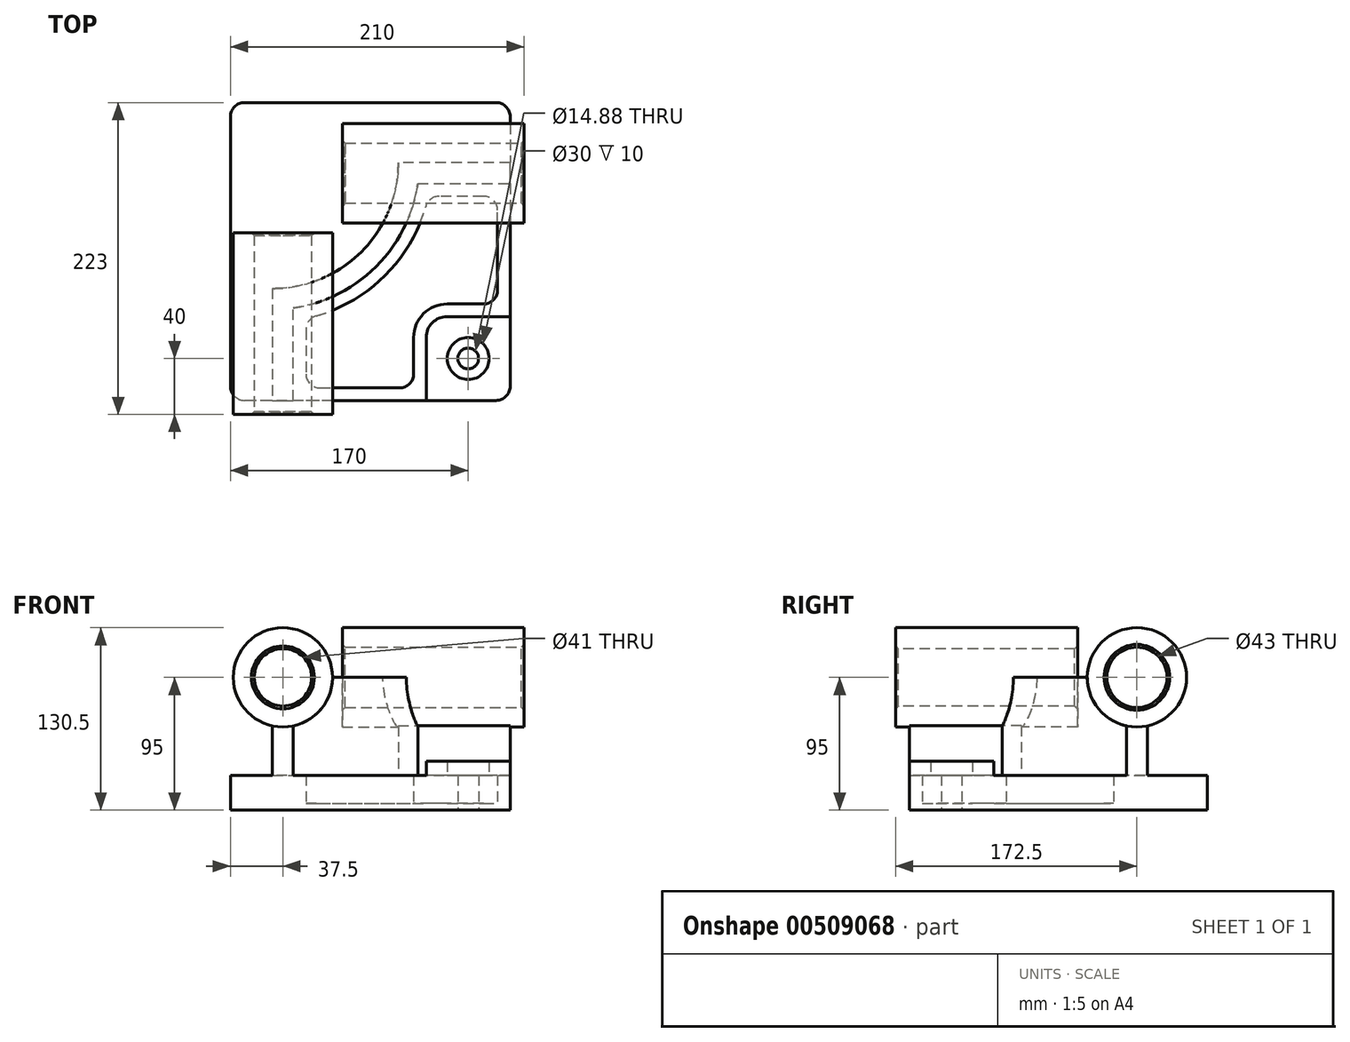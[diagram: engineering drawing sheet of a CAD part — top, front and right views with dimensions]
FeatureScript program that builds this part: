
annotation { "Feature Type Name" : "Feature", "Feature Type Description" : "" }
export const myFeature = defineFeature(function(context is Context, id is Id, definition is map)
    precondition{}
    {
        {
            var Q0;
            Q0=qCreatedBy(makeId("Top.planeOp"),FACE);
            var sketch = newSketch(context, id + "F0", { "sketchPlane" : qUnion([Q0])});
            skLineSegment(sketch, "E0.bottom", {"start": v(-10, 0) * mm, "end": v(-190, 0) * mm});
            skLineSegment(sketch, "E0.top", {"start": v(-10, -213) * mm, "end": v(-190, -213) * mm});
            skLineSegment(sketch, "E0.left", {"start": v(0, -10) * mm, "end": v(0, -203) * mm});
            skLineSegment(sketch, "E0.right", {"start": v(-200, -10) * mm, "end": v(-200, -203) * mm});
            skPoint(sketch, "E1.visualSharp", {"position": v(-200, -213) * mm});
            skArc(sketch, "E1.filletArc", {"start": v(-200, -203) * mm, "mid": v(-197.07, -210.07) * mm, "end": v(-190, -213) * mm});
            skPoint(sketch, "E2.visualSharp", {"position": v(-200, 0) * mm});
            skArc(sketch, "E2.filletArc", {"start": v(-190, 0) * mm, "mid": v(-197.07, -2.93) * mm, "end": v(-200, -10) * mm});
            skPoint(sketch, "E3.visualSharp", {"position": v(0, 0) * mm});
            skArc(sketch, "E3.filletArc", {"start": v(0, -10) * mm, "mid": v(-2.93, -2.93) * mm, "end": v(-10, 0) * mm});
            skPoint(sketch, "E4.visualSharp", {"position": v(0, -213) * mm});
            skArc(sketch, "E4.filletArc", {"start": v(-10, -213) * mm, "mid": v(-2.93, -210.07) * mm, "end": v(0, -203) * mm});
            skSolve(sketch);
        }
        {
            var Q0;
            Q0 = qSketchRegion(id + "F0", true);
            extrude(context, id + "F1", {"entities" : qUnion([Q0]), "depth" : 25 * mm});
        }
        {
            var Q0;
            Q0=qCreatedBy(makeId("Top.planeOp"),FACE);
            var sketch = newSketch(context, id + "F2", { "sketchPlane" : qUnion([Q0])});
            skLineSegment(sketch, "E5", {"start": v(-170, -213) * mm, "end": v(-170, -133) * mm});
            skLineSegment(sketch, "E6", {"start": v(-80, -43) * mm, "end": v(0, -43) * mm});
            skLineSegment(sketch, "E7", {"start": v(0, -43) * mm, "end": v(0, -58) * mm});
            skLineSegment(sketch, "E8", {"start": v(0, -58) * mm, "end": v(-66.08, -58) * mm});
            skLineSegment(sketch, "E9", {"start": v(-155, -146.92) * mm, "end": v(-155, -213) * mm});
            skLineSegment(sketch, "E10", {"start": v(-155, -213) * mm, "end": v(-170, -213) * mm});
            skArc(sketch, "E11", {"start": v(-155, -146.92) * mm, "mid": v(-95.75, -117.25) * mm, "end": v(-66.08, -58) * mm});
            skArc(sketch, "E12", {"start": v(-170, -133) * mm, "mid": v(-106.36, -106.64) * mm, "end": v(-80, -43) * mm});
            skLineSegment(sketch, "E13", {"start": v(-170, -43) * mm, "end": v(-107.14, -107.41) * mm, "construction": true});
            skLineSegment(sketch, "E14", {"start": v(-107.14, -107.41) * mm, "end": v(-96.67, -118.15) * mm, "construction": true});
            skSolve(sketch);
        }
        {
            var Q0;
            Q0 = qSketchRegion(id + "F2", true);
            extrude(context, id + "F3", {"entities" : qUnion([Q0]), "operationType" : NewBodyOperationType.ADD, "depth" : 95 * mm});
        }
        {
            var Q0;
            Q0=makeQuery(id+"F3.boolean.opBoolean","MERGE",FACE,{"derivedFrom":[makeQuery(id+"F1.opExtrude","SWEPT_FACE",FACE,{"disambiguationData":[OSD([sQuery(id+"F0.wireOp",EDGE,"E0.top")])]}),makeQuery(id+"F3.opExtrude","SWEPT_FACE",FACE,{"disambiguationData":[OSD([sQuery(id+"F2.wireOp",EDGE,"E10")])]})]});
            cPlane(context, id + "F4", {"entities" : qUnion([Q0]), "cplaneType" : CPlaneType.OFFSET, "offset" : 10 * mm, "width" : 150 * mm, "height" : 150 * mm});
        }
        {
            var Q0;
            Q0=makeQuery(id+"F3.boolean.opBoolean","MERGE",FACE,{"derivedFrom":[makeQuery(id+"F1.opExtrude","SWEPT_FACE",FACE,{"disambiguationData":[OSD([sQuery(id+"F0.wireOp",EDGE,"E0.left")])]}),makeQuery(id+"F3.opExtrude","SWEPT_FACE",FACE,{"disambiguationData":[OSD([sQuery(id+"F2.wireOp",EDGE,"E7")])]})]});
            cPlane(context, id + "F5", {"entities" : qUnion([Q0]), "cplaneType" : CPlaneType.OFFSET, "offset" : 10 * mm, "width" : 150 * mm, "height" : 150 * mm});
        }
        {
            var Q0;
            Q0=qCreatedBy(id+"F4.planeOp",FACE);
            var sketch = newSketch(context, id + "F6", { "sketchPlane" : qUnion([Q0])});
            skCircle(sketch, "E15", {"center": v(-162.5, 95) * mm, "radius": 35.5 * mm});
            skSolve(sketch);
        }
        {
            var Q0;
            Q0 = qSketchRegion(id + "F6", true);
            extrude(context, id + "F7", {"entities" : qUnion([Q0]), "operationType" : NewBodyOperationType.ADD, "oppositeDirection" : true, "depth" : 130 * mm});
        }
        {
            var Q0;
            Q0=qCreatedBy(id+"F5.planeOp",FACE);
            var sketch = newSketch(context, id + "F8", { "sketchPlane" : qUnion([Q0])});
            skCircle(sketch, "E16", {"center": v(-50.5, 95) * mm, "radius": 35.5 * mm});
            skSolve(sketch);
        }
        {
            var Q0;
            Q0 = qSketchRegion(id + "F8", true);
            extrude(context, id + "F9", {"entities" : qUnion([Q0]), "operationType" : NewBodyOperationType.ADD, "oppositeDirection" : true, "depth" : 130 * mm});
        }
        {
            var Q0;
            Q0=makeQuery(id+"F3.opExtrude","CAP_FACE",FACE,{"disambiguationData":[OSD([sQuery(id+"F2.wireOp",EDGE,"E5"),sQuery(id+"F2.wireOp",EDGE,"E6"),sQuery(id+"F2.wireOp",EDGE,"E7"),sQuery(id+"F2.wireOp",EDGE,"E8"),sQuery(id+"F2.wireOp",EDGE,"E9"),sQuery(id+"F2.wireOp",EDGE,"E10"),sQuery(id+"F2.wireOp",EDGE,"E11"),sQuery(id+"F2.wireOp",EDGE,"E12")])],"isStart":false});
            var sketch = newSketch(context, id + "F10", { "sketchPlane" : qUnion([Q0])});
            skLineSegment(sketch, "E17.0", {"start": v(-127, -223) * mm, "end": v(-198, -223) * mm, "construction": true});
            skLineSegment(sketch, "E18.0", {"start": v(-127, -93) * mm, "end": v(-198, -93) * mm, "construction": true});
            skLineSegment(sketch, "E19", {"start": v(-162.5, -223) * mm, "end": v(-162.5, -93) * mm});
            skLineSegment(sketch, "E20", {"start": v(-162.5, -223) * mm, "end": v(-185, -223) * mm});
            skLineSegment(sketch, "E21", {"start": v(-185, -223) * mm, "end": v(-185, -93) * mm, "construction": true});
            skLineSegment(sketch, "E22", {"start": v(-185, -93) * mm, "end": v(-162.5, -93) * mm});
            skLineSegment(sketch, "E23", {"start": v(-185, -223) * mm, "end": v(-183, -221) * mm});
            skLineSegment(sketch, "E24", {"start": v(-183, -221) * mm, "end": v(-183, -95) * mm});
            skLineSegment(sketch, "E25", {"start": v(-183, -95) * mm, "end": v(-185, -93) * mm});
            skLineSegment(sketch, "E26", {"start": v(-162.5, -223) * mm, "end": v(-162.5, -264.32) * mm, "construction": true});
            skSolve(sketch);
        }
        {
            var Q0;
            Q0 = qSketchRegion(id + "F10", true);
            var Q1;
            Q1=sQuery(id+"F10.wireOp",EDGE,"E26");
            revolve(context, id + "F11", {"operationType" : NewBodyOperationType.REMOVE, "entities" : qUnion([Q0]), "axis" : qUnion([Q1]), "revolveType" : RevolveType.FULL, "oppositeDirection" : true});
        }
        {
            var Q0;
            Q0=makeQuery(id+"F3.opExtrude","CAP_FACE",FACE,{"disambiguationData":[OSD([sQuery(id+"F2.wireOp",EDGE,"E5"),sQuery(id+"F2.wireOp",EDGE,"E6"),sQuery(id+"F2.wireOp",EDGE,"E7"),sQuery(id+"F2.wireOp",EDGE,"E8"),sQuery(id+"F2.wireOp",EDGE,"E9"),sQuery(id+"F2.wireOp",EDGE,"E10"),sQuery(id+"F2.wireOp",EDGE,"E11"),sQuery(id+"F2.wireOp",EDGE,"E12")])],"isStart":false});
            var sketch = newSketch(context, id + "F12", { "sketchPlane" : qUnion([Q0])});
            skLineSegment(sketch, "E27.0", {"start": v(-120, -15) * mm, "end": v(-120, -86) * mm, "construction": true});
            skLineSegment(sketch, "E28.0", {"start": v(10, -15) * mm, "end": v(10, -86) * mm, "construction": true});
            skLineSegment(sketch, "E29", {"start": v(-120, -50.5) * mm, "end": v(10, -50.5) * mm});
            skLineSegment(sketch, "E30", {"start": v(-120, -50.5) * mm, "end": v(-120, -74) * mm});
            skLineSegment(sketch, "E31", {"start": v(-120, -74) * mm, "end": v(10, -74) * mm, "construction": true});
            skLineSegment(sketch, "E32", {"start": v(10, -74) * mm, "end": v(10, -50.5) * mm});
            skLineSegment(sketch, "E33", {"start": v(-120, -74) * mm, "end": v(-118, -72) * mm});
            skLineSegment(sketch, "E34", {"start": v(-118, -72) * mm, "end": v(8, -72) * mm});
            skLineSegment(sketch, "E35", {"start": v(8, -72) * mm, "end": v(10, -74) * mm});
            skLineSegment(sketch, "E36", {"start": v(10, -50.5) * mm, "end": v(28.45, -50.5) * mm, "construction": true});
            skSolve(sketch);
        }
        {
            var Q0;
            Q0 = qSketchRegion(id + "F12", true);
            var Q1;
            Q1=sQuery(id+"F12.wireOp",EDGE,"E36");
            revolve(context, id + "F13", {"operationType" : NewBodyOperationType.REMOVE, "entities" : qUnion([Q0]), "axis" : qUnion([Q1]), "revolveType" : RevolveType.FULL, "oppositeDirection" : true});
        }
        {
            var Q0;
            Q0=qCreatedBy(makeId("Top.planeOp"),FACE);
            var sketch = newSketch(context, id + "F14", { "sketchPlane" : qUnion([Q0])});
            skLineSegment(sketch, "E37.0", {"start": v(-10, -213) * mm, "end": v(-60, -213) * mm});
            skPoint(sketch, "E38.0", {"position": v(-2.93, -210.07) * mm});
            skLineSegment(sketch, "E39.0", {"start": v(0, -153) * mm, "end": v(0, -203) * mm});
            skArc(sketch, "E40.0", {"start": v(-10, -213) * mm, "mid": v(-2.93, -210.07) * mm, "end": v(0, -203) * mm});
            skLineSegment(sketch, "E41", {"start": v(-60, -213) * mm, "end": v(-60, -168) * mm});
            skLineSegment(sketch, "E42", {"start": v(-45, -153) * mm, "end": v(0, -153) * mm});
            skPoint(sketch, "E43.orphan", {"position": v(-155, -213) * mm});
            skArc(sketch, "E44", {"start": v(-45, -153) * mm, "mid": v(-55.6, -157.4) * mm, "end": v(-60, -168) * mm});
            skPoint(sketch, "E45.orphan", {"position": v(0, -58) * mm});
            skSolve(sketch);
        }
        {
            var Q0;
            Q0 = qSketchRegion(id + "F14", true);
            extrude(context, id + "F15", {"entities" : qUnion([Q0]), "operationType" : NewBodyOperationType.ADD, "depth" : 35 * mm});
        }
        {
            var Q0;
            Q0=qCreatedBy(makeId("Right.planeOp"),FACE);
            cPlane(context, id + "F16", {"entities" : qUnion([Q0]), "cplaneType" : CPlaneType.OFFSET, "offset" : 30 * mm, "oppositeDirection" : true, "width" : 150 * mm, "height" : 150 * mm});
        }
        {
            var Q0;
            Q0=qCreatedBy(id+"F16.planeOp",FACE);
            var sketch = newSketch(context, id + "F17", { "sketchPlane" : qUnion([Q0])});
            skLineSegment(sketch, "E46", {"start": v(-183, 79.02) * mm, "end": v(-183, -100.5) * mm});
            skLineSegment(sketch, "E47", {"start": v(-183, -100.5) * mm, "end": v(-175.56, -100.5) * mm});
            skLineSegment(sketch, "E48", {"start": v(-175.56, -100.5) * mm, "end": v(-175.56, 25) * mm});
            skLineSegment(sketch, "E49", {"start": v(-175.56, 25) * mm, "end": v(-168, 25) * mm});
            skLineSegment(sketch, "E50", {"start": v(-168, 25) * mm, "end": v(-168, 79.02) * mm});
            skLineSegment(sketch, "E51", {"start": v(-168, 79.02) * mm, "end": v(-183, 79.02) * mm});
            skLineSegment(sketch, "E52", {"start": v(-183, -100.5) * mm, "end": v(-183, -118.63) * mm, "construction": true});
            skSolve(sketch);
        }
        {
            var Q0;
            Q0 = qSketchRegion(id + "F17", true);
            var Q1;
            Q1=sQuery(id+"F17.wireOp",EDGE,"E52");
            revolve(context, id + "F18", {"operationType" : NewBodyOperationType.REMOVE, "entities" : qUnion([Q0]), "axis" : qUnion([Q1]), "revolveType" : RevolveType.FULL, "oppositeDirection" : true});
        }
        {
            var Q0;
            Q0=qCreatedBy(makeId("Top.planeOp"),FACE);
            cPlane(context, id + "F19", {"entities" : qUnion([Q0]), "cplaneType" : CPlaneType.OFFSET, "offset" : 5 * mm, "width" : 150 * mm, "height" : 150 * mm});
        }
        {
            var Q0;
            Q0=qCreatedBy(id+"F19.planeOp",FACE);
            var sketch = newSketch(context, id + "F20", { "sketchPlane" : qUnion([Q0])});
            skLineSegment(sketch, "E53.0.0", {"start": v(-45, -153) * mm, "end": v(0, -153) * mm, "construction": true});
            skLineSegment(sketch, "E53.0.1", {"start": v(0, -153) * mm, "end": v(0, -58) * mm, "construction": true});
            skLineSegment(sketch, "E53.0.2", {"start": v(0, -58) * mm, "end": v(-66.08, -58) * mm, "construction": true});
            skArc(sketch, "E53.0.3", {"start": v(-66.08, -58) * mm, "mid": v(-95.75, -117.25) * mm, "end": v(-155, -146.92) * mm, "construction": true});
            skLineSegment(sketch, "E53.0.4", {"start": v(-155, -146.92) * mm, "end": v(-155, -213) * mm, "construction": true});
            skLineSegment(sketch, "E53.0.5", {"start": v(-155, -213) * mm, "end": v(-60, -213) * mm, "construction": true});
            skLineSegment(sketch, "E53.0.6", {"start": v(-60, -213) * mm, "end": v(-60, -168) * mm, "construction": true});
            skArc(sketch, "E53.0.7", {"start": v(-60, -168) * mm, "mid": v(-55.6, -157.4) * mm, "end": v(-45, -153) * mm, "construction": true});
            skArc(sketch, "E54.0", {"start": v(-60.37, -74.26) * mm, "mid": v(-89.39, -123.61) * mm, "end": v(-138.74, -152.63) * mm});
            skLineSegment(sketch, "E54.1", {"start": v(-19, -67) * mm, "end": v(-50.75, -67) * mm});
            skLineSegment(sketch, "E54.2", {"start": v(-146, -162.25) * mm, "end": v(-146, -194) * mm});
            skLineSegment(sketch, "E54.3", {"start": v(-9, -134) * mm, "end": v(-9, -77) * mm});
            skLineSegment(sketch, "E54.4", {"start": v(-136, -204) * mm, "end": v(-79, -204) * mm});
            skLineSegment(sketch, "E54.5", {"start": v(-69, -194) * mm, "end": v(-69, -168) * mm});
            skArc(sketch, "E54.6", {"start": v(-69, -168) * mm, "mid": v(-61.97, -151.03) * mm, "end": v(-45, -144) * mm});
            skLineSegment(sketch, "E54.7", {"start": v(-45, -144) * mm, "end": v(-19, -144) * mm});
            skPoint(sketch, "E55.visualSharp", {"position": v(-146, -154.45) * mm});
            skArc(sketch, "E55.filletArc", {"start": v(-138.74, -152.63) * mm, "mid": v(-143.98, -156.22) * mm, "end": v(-146, -162.25) * mm});
            skPoint(sketch, "E56.visualSharp", {"position": v(-146, -204) * mm});
            skArc(sketch, "E56.filletArc", {"start": v(-146, -194) * mm, "mid": v(-143.07, -201.07) * mm, "end": v(-136, -204) * mm});
            skPoint(sketch, "E57.visualSharp", {"position": v(-69, -204) * mm});
            skArc(sketch, "E57.filletArc", {"start": v(-79, -204) * mm, "mid": v(-71.93, -201.07) * mm, "end": v(-69, -194) * mm});
            skPoint(sketch, "E58.visualSharp", {"position": v(-9, -144) * mm});
            skArc(sketch, "E58.filletArc", {"start": v(-19, -144) * mm, "mid": v(-11.93, -141.07) * mm, "end": v(-9, -134) * mm});
            skPoint(sketch, "E59.visualSharp", {"position": v(-9, -67) * mm});
            skArc(sketch, "E59.filletArc", {"start": v(-9, -77) * mm, "mid": v(-11.93, -69.93) * mm, "end": v(-19, -67) * mm});
            skPoint(sketch, "E60.visualSharp", {"position": v(-58.55, -67) * mm});
            skArc(sketch, "E60.filletArc", {"start": v(-50.75, -67) * mm, "mid": v(-56.78, -69.02) * mm, "end": v(-60.37, -74.26) * mm});
            skSolve(sketch);
        }
        {
            var Q0;
            Q0 = qSketchRegion(id + "F20", true);
            var Q1;
            {var subQ0=sQuery(id+"F0.wireOp",EDGE,"E4.filletArc");var subQ1=sQuery(id+"F0.wireOp",EDGE,"E0.left");var subQ2=sQuery(id+"F0.wireOp",EDGE,"E0.top");Q1=makeQuery(id+"F3.boolean.opBoolean","SPLIT",FACE,{"disambiguationData":[TD([makeQuery(id+"F1.opExtrude","SWEPT_FACE",FACE,{"disambiguationData":[OSD([subQ0])]})])],"derivedFrom":makeQuery(id+"F1.opExtrude","CAP_FACE",FACE,{"disambiguationData":[OSD([sQuery(id+"F0.wireOp",EDGE,"E0.bottom"),subQ2,subQ1,sQuery(id+"F0.wireOp",EDGE,"E0.right"),sQuery(id+"F0.wireOp",EDGE,"E1.filletArc"),sQuery(id+"F0.wireOp",EDGE,"E2.filletArc"),sQuery(id+"F0.wireOp",EDGE,"E3.filletArc"),subQ0])],"isStart":false})});}
            extrude(context, id + "F21", {"entities" : qUnion([Q0]), "operationType" : NewBodyOperationType.REMOVE, "endBound" : BoundingType.UP_TO_SURFACE, "endBoundEntityFace" : qUnion([Q1]), "depth" : 25 * mm});
        }
    });
